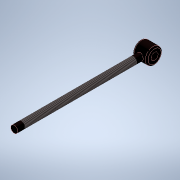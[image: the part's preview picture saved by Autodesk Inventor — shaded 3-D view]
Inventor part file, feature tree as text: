
AUTODESK INVENTOR PART (.ipt)
format: ipt  version: 2021 (Build 250183000, 183)  size: 120,832 bytes
history: native  units: mm
features: extrude x3, sketch x3, thread x1, fillet x1
ambient origin geometry x8: Origin, YZ Plane, XZ Plane, XY Plane, X Axis, Y Axis, Z Axis, Center Point
bodies: Solid1 (feature_tree)
feature tree (8):
  extrude  "Extrusion1"  Depth=10.0mm TaperAngle=0.0deg
  thread  "Thread1"  [1 undecoded]
  extrude  "Extrusion2"  Depth=10.0mm
  extrude  "Extrusion3"  Depth=2.0mm
  fillet  "Fillet1"  [1 undecoded]
  sketch  "Sketch1"  dims[d0=10.0mm d1=180.0mm d2=0.0mm d3=160.0mm d4=10.0mm]
  sketch  "Sketch2"  dims[d5=20.0mm d6=0.0mm d7=10.0mm]
  sketch  "Sketch3"  dims[d8=20.0mm d9=0.0mm d10=2.0mm]
note: 2 required parameter values undecoded (feature->parameter linkage not recoverable at this tier; creation-order binding heuristic only, values carry confidence <= 0.55)
